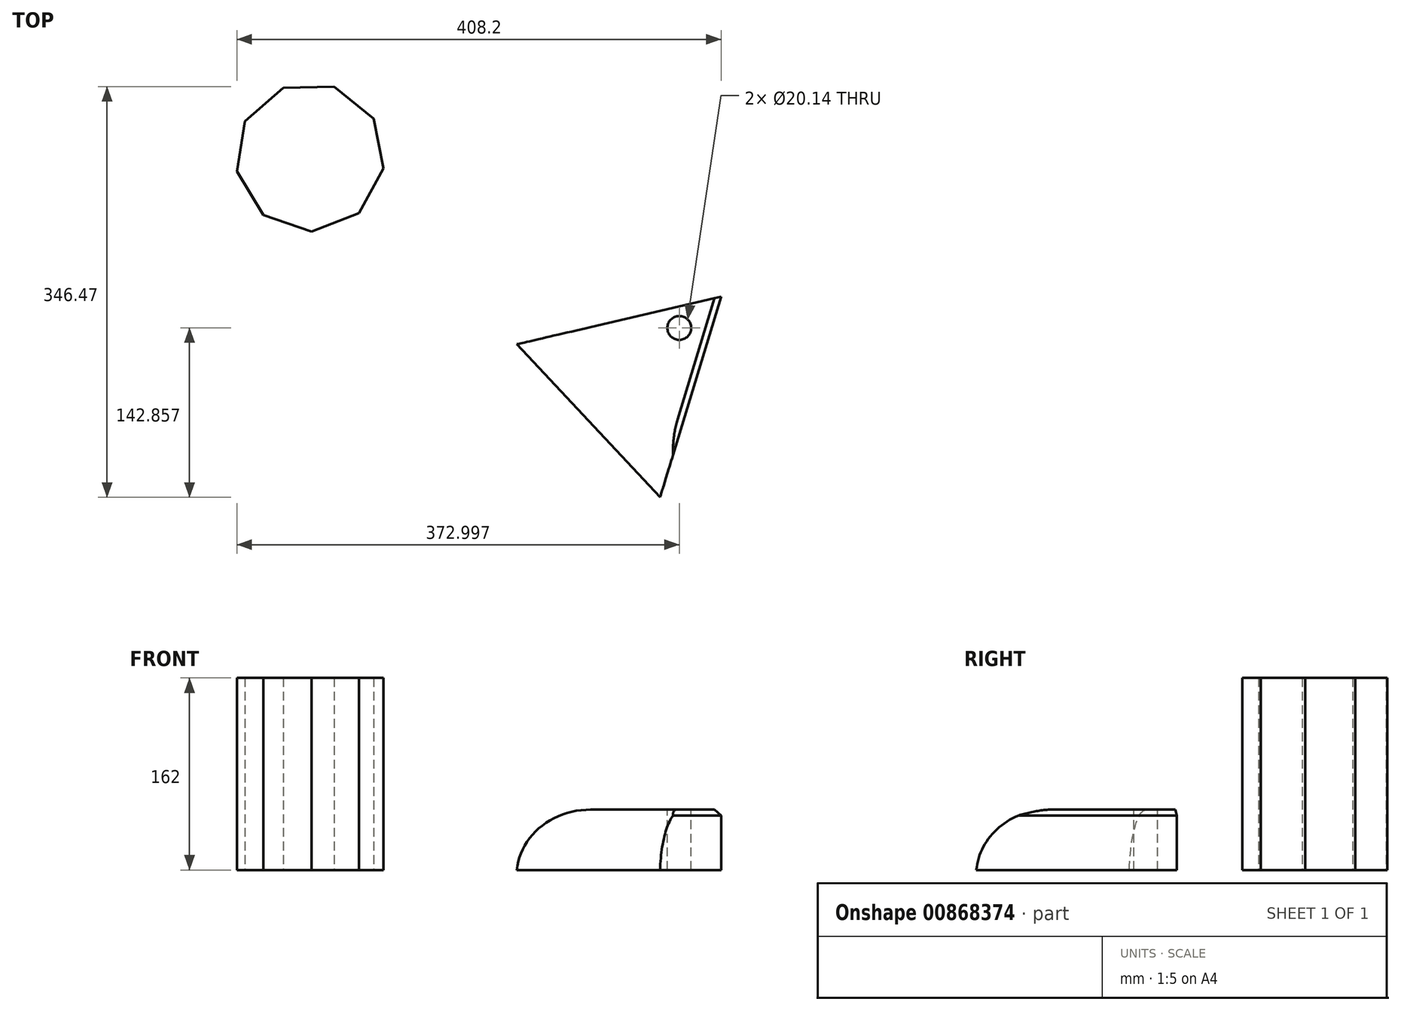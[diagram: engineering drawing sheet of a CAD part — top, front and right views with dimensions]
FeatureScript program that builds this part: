
annotation { "Feature Type Name" : "Feature", "Feature Type Description" : "" }
export const myFeature = defineFeature(function(context is Context, id is Id, definition is map)
    precondition{}
    {
        {
            var Q0;
            Q0=qCreatedBy(makeId("Top.planeOp"),FACE);
            var sketch = newSketch(context, id + "F0", { "sketchPlane" : qUnion([Q0])});
            skCircle(sketch, "E0.cCircle", {"center": v(-89.98, 8.19) * mm, "radius": 51.05 * mm, "construction": true});
            skLineSegment(sketch, "E0.0", {"start": v(-15.44, 77.95) * mm, "end": v(-66.83, -91.25) * mm});
            skLineSegment(sketch, "E0.1", {"start": v(-66.83, -91.25) * mm, "end": v(-187.67, 37.86) * mm});
            skLineSegment(sketch, "E0.2", {"start": v(-187.67, 37.86) * mm, "end": v(-15.44, 77.95) * mm});
            skPoint(sketch, "E0.0.midPoint", {"position": v(-41.14, -6.65) * mm});
            skSolve(sketch);
        }
        {
            var Q0;
            Q0 = qSketchRegion(id + "F0", true);
            extrude(context, id + "F1", {"entities" : qUnion([Q0]), "depth" : 51 * mm, "offsetDistance" : 25 * mm});
        }
        {
            var Q0;
            Q0=makeQuery(id+"F1.opExtrude","CAP_EDGE",EDGE,{"disambiguationData":[OSD([sQuery(id+"F0.wireOp",EDGE,"E0.0")])],"isStart":false});
            chamfer(context, id + "F2", {"entities" : qUnion([Q0]), "width" : 5 * mm, "tangentPropagation" : true});
        }
        {
            var Q0;
            Q0=makeQuery(id+"F1.opExtrude","CAP_EDGE",EDGE,{"disambiguationData":[OSD([sQuery(id+"F0.wireOp",EDGE,"E0.1")])],"isStart":false});
            fillet(context, id + "F3", {"entities" : qUnion([Q0]), "radius" : 55.53 * mm, "tangentPropagation" : true, "allowEdgeOverflow" : false});
        }
        {
            var Q0;
            Q0=makeQuery(id+"F1.opExtrude","CAP_FACE",FACE,{"disambiguationData":[OSD([sQuery(id+"F0.wireOp",EDGE,"E0.0"),sQuery(id+"F0.wireOp",EDGE,"E0.1"),sQuery(id+"F0.wireOp",EDGE,"E0.2")])],"isStart":false});
            var sketch = newSketch(context, id + "F4", { "sketchPlane" : qUnion([Q0])});
            skCircle(sketch, "E1", {"center": v(-50.64, 51.6) * mm, "radius": 10.07 * mm});
            skSolve(sketch);
        }
        {
            var Q0;
            Q0 = qSketchRegion(id + "F4", true);
            extrude(context, id + "F5", {"entities" : qUnion([Q0]), "operationType" : NewBodyOperationType.REMOVE, "oppositeDirection" : true, "depth" : 111 * mm, "offsetDistance" : 25 * mm});
        }
        {
            var Q0;
            Q0=qCreatedBy(makeId("Top.planeOp"),FACE);
            var sketch = newSketch(context, id + "F6", { "sketchPlane" : qUnion([Q0])});
            skCircle(sketch, "E2.cCircle", {"center": v(-362.03, 195.8) * mm, "radius": 59 * mm, "construction": true});
            skLineSegment(sketch, "E2.0", {"start": v(-320.7, 148.52) * mm, "end": v(-360.76, 133.02) * mm});
            skLineSegment(sketch, "E2.1", {"start": v(-360.76, 133.02) * mm, "end": v(-401.41, 146.9) * mm});
            skLineSegment(sketch, "E2.2", {"start": v(-401.41, 146.9) * mm, "end": v(-423.64, 183.65) * mm});
            skLineSegment(sketch, "E2.3", {"start": v(-423.64, 183.65) * mm, "end": v(-417.03, 226.09) * mm});
            skLineSegment(sketch, "E2.4", {"start": v(-417.03, 226.09) * mm, "end": v(-384.7, 254.36) * mm});
            skLineSegment(sketch, "E2.5", {"start": v(-384.7, 254.36) * mm, "end": v(-341.75, 255.22) * mm});
            skLineSegment(sketch, "E2.6", {"start": v(-341.75, 255.22) * mm, "end": v(-308.3, 228.28) * mm});
            skLineSegment(sketch, "E2.7", {"start": v(-308.3, 228.28) * mm, "end": v(-299.98, 186.14) * mm});
            skLineSegment(sketch, "E2.8", {"start": v(-299.98, 186.14) * mm, "end": v(-320.7, 148.52) * mm});
            skPoint(sketch, "E2.0.midPoint", {"position": v(-340.73, 140.77) * mm});
            skSolve(sketch);
        }
        {
            var Q0;
            Q0 = qSketchRegion(id + "F6", true);
            extrude(context, id + "F7", {"entities" : qUnion([Q0]), "depth" : 162 * mm, "offsetDistance" : 25 * mm});
        }
    });
